FCSTD DOCUMENT  (FreeCAD 0.21R31641 (Git))
Label: пенопласт2
License: All rights reserved
LicenseURL: http://en.wikipedia.org/wiki/All_rights_reserved
objects: Sketcher::SketchObject×3, PartDesign::Body×1
note: 4 computed .brp shape members not serialized (recipe doc carries the construction recipe); baked Part::Feature solids carry a one-line shape summary decoded from their .brp

FEATURE [Sketcher::SketchObject] Sketch
  FullyConstrained = false
  MapMode = 5
  Support = -> [XY_Plane]
  sketch-geometry (4):
    g0: ArcOfCircle CenterX=0 CenterY=0 CenterZ=0 NormalX=0 NormalY=0 NormalZ=1 AngleXU=0 Radius=63.8808 StartAngle=5.73869 EndAngle=10.1634
    g1: ArcOfCircle CenterX=0 CenterY=0 CenterZ=0 NormalX=0 NormalY=0 NormalZ=1 AngleXU=0 Radius=81.6622 StartAngle=5.72839 EndAngle=10.1499
    g2: LineSegment StartX=-61.1188 StartY=-54.159 StartZ=0 EndX=-47.2313 EndY=-43.0112 EndZ=0
    g3: LineSegment StartX=54.6429 StartY=-33.0894 StartZ=0 EndX=69.4135 EndY=-43.0173 EndZ=0
  constraints (6):
    c: Coincident(g0,g-1)
    c: Coincident(g1,g0)
    c: Coincident(g2,g1)
    c: Coincident(g2,g0)
    c: Coincident(g3,g0)
    c: Coincident(g3,g1)
FEATURE [Sketcher::SketchObject] Sketch001
  FullyConstrained = false
  MapMode = 5
  Support = -> [XY_Plane]
  sketch-geometry (5):
    g0: LineSegment StartX=-86.0699 StartY=-86.0699 StartZ=0 EndX=-86.0699 EndY=86.0699 EndZ=0
    g1: LineSegment StartX=-86.0699 StartY=86.0699 StartZ=0 EndX=86.0699 EndY=86.0699 EndZ=0
    g2: LineSegment StartX=86.0699 StartY=86.0699 StartZ=0 EndX=86.0699 EndY=-86.0699 EndZ=0
    g3: LineSegment StartX=86.0699 StartY=-86.0699 StartZ=0 EndX=-86.0699 EndY=-86.0699 EndZ=0
    g4: GeomPoint X=-1e-16 Y=3e-16 Z=0
  constraints (11):
    c: Coincident(g0,g1)
    c: Coincident(g1,g2)
    c: Coincident(g2,g3)
    c: Coincident(g3,g0)
    c: Horizontal(g1)
    c: Horizontal(g3)
    c: Vertical(g0)
    c: Vertical(g2)
    c: Symmetric(g1,g0,g4)
    c: Coincident(g4,g-1)
    c: Equal(g2,g1)
FEATURE [Sketcher::SketchObject] Sketch002
  FullyConstrained = true
  MapMode = 5
  Support = -> [XY_Plane]
FEATURE [PartDesign::Body] Body
  Group = -> [Sketch,Sketch001,Sketch002]
  Origin = -> Origin
